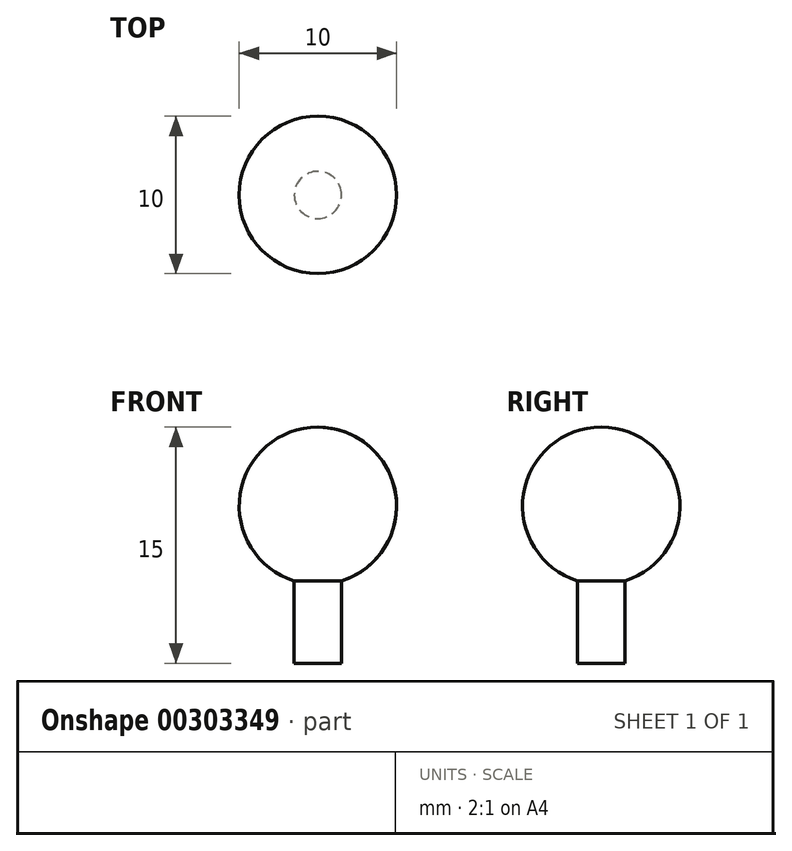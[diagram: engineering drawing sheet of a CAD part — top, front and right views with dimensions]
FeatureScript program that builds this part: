
annotation { "Feature Type Name" : "Feature", "Feature Type Description" : "" }
export const myFeature = defineFeature(function(context is Context, id is Id, definition is map)
    precondition{}
    {
        {
            var Q0;
            Q0=qCreatedBy(makeId("Front.planeOp"),FACE);
            var sketch = newSketch(context, id + "F0", { "sketchPlane" : qUnion([Q0])});
            skArc(sketch, "E0", {"start": v(1.5, -4.77) * mm, "mid": v(4.94, 0.76) * mm, "end": v(0, 5) * mm});
            skLineSegment(sketch, "E1.top", {"start": v(1.5, -10) * mm, "end": v(0, -10) * mm});
            skLineSegment(sketch, "E1.left", {"start": v(1.5, -4.77) * mm, "end": v(1.5, -10) * mm});
            skPoint(sketch, "E2.orphan", {"position": v(-1.5, 10) * mm});
            skPoint(sketch, "E3.orphan", {"position": v(1.5, 10) * mm});
            skLineSegment(sketch, "E4", {"start": v(0, 5) * mm, "end": v(0, -10) * mm});
            skPoint(sketch, "E5.orphan", {"position": v(-1.5, -10) * mm});
            skSolve(sketch);
        }
        {
            var Q0;
            Q0 = qSketchRegion(id + "F0", true);
            var Q1;
            Q1=sQuery(id+"F0.wireOp",EDGE,"E4");
            revolve(context, id + "F1", {"entities" : qUnion([Q0]), "axis" : qUnion([Q1]), "revolveType" : RevolveType.FULL});
        }
    });
